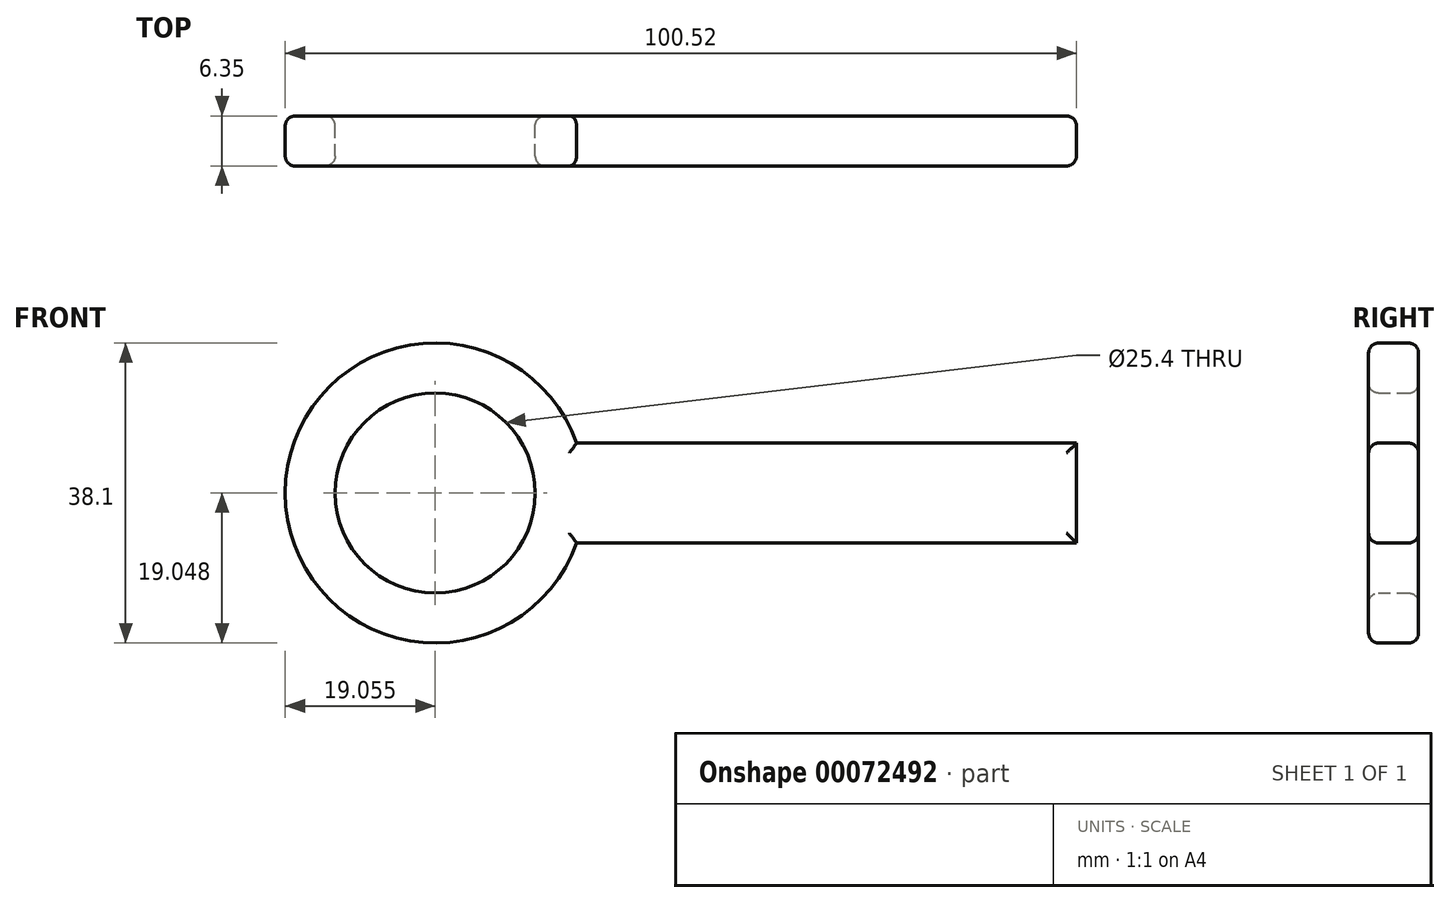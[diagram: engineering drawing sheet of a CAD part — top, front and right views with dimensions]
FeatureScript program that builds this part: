
annotation { "Feature Type Name" : "Feature", "Feature Type Description" : "" }
export const myFeature = defineFeature(function(context is Context, id is Id, definition is map)
    precondition{}
    {
        {
            var Q0;
            Q0=qCreatedBy(makeId("Front.planeOp"),FACE);
            var sketch = newSketch(context, id + "F0", { "sketchPlane" : qUnion([Q0])});
            skCircle(sketch, "E0", {"center": v(-45.07, 42.75) * mm, "radius": 19.05 * mm});
            skLineSegment(sketch, "E1", {"start": v(-27.1, 36.4) * mm, "end": v(36.4, 36.4) * mm});
            skLineSegment(sketch, "E2", {"start": v(-27.1, 49.1) * mm, "end": v(36.4, 49.1) * mm});
            skLineSegment(sketch, "E3", {"start": v(36.4, 49.1) * mm, "end": v(36.4, 36.4) * mm});
            skCircle(sketch, "E4", {"center": v(-45.07, 42.75) * mm, "radius": 12.7 * mm});
            skLineSegment(sketch, "E5.bottom", {"start": v(26.7, 36.4) * mm, "end": v(20.35, 36.4) * mm});
            skLineSegment(sketch, "E5.top", {"start": v(26.7, 17.35) * mm, "end": v(20.35, 17.35) * mm});
            skLineSegment(sketch, "E5.left", {"start": v(26.7, 36.4) * mm, "end": v(26.7, 17.35) * mm});
            skLineSegment(sketch, "E5.right", {"start": v(20.35, 36.4) * mm, "end": v(20.35, 17.35) * mm});
            skPoint(sketch, "E6.oppositeSnap0", {"position": v(4.65, 36.4) * mm});
            skLineSegment(sketch, "E6.bottom", {"start": v(11, 36.4) * mm, "end": v(4.65, 36.4) * mm});
            skLineSegment(sketch, "E6.top", {"start": v(11, 17.35) * mm, "end": v(4.65, 17.35) * mm});
            skLineSegment(sketch, "E6.left", {"start": v(11, 36.4) * mm, "end": v(11, 17.35) * mm});
            skLineSegment(sketch, "E6.right", {"start": v(4.65, 36.4) * mm, "end": v(4.65, 17.35) * mm});
            skSolve(sketch);
        }
        {
            var Q0;
            Q0=makeQuery(id+"F0.imprint","IMPRINT",FACE,{"disambiguationData":[TD([[makeQuery(id+"F0.imprint","IMPRINT",EDGE,{"derivedFrom":sQuery(id+"F0.wireOp",EDGE,"E5.bottom")}),1.0]])]});
            var Q1;
            Q1=makeQuery(id+"F0.imprint","IMPRINT",FACE,{"disambiguationData":[TD([[makeQuery(id+"F0.imprint","IMPRINT",EDGE,{"derivedFrom":sQuery(id+"F0.wireOp",EDGE,"E4")}),-1.0]])]});
            var Q2;
            {var subQ6=sQuery(id+"F0.wireOp",EDGE,"E2");Q2=makeQuery(id+"F0.imprint","IMPRINT",FACE,{"disambiguationData":[TD([[makeQuery(id+"F0.imprint","IMPRINT",EDGE,{"derivedFrom":subQ6}),-1.0]])]});}
            var Q3;
            Q3=makeQuery(id+"F0.imprint","IMPRINT",FACE,{"disambiguationData":[TD([[makeQuery(id+"F0.imprint","IMPRINT",EDGE,{"derivedFrom":sQuery(id+"F0.wireOp",EDGE,"E6.bottom")}),1.0]])]});
            extrude(context, id + "F1", {"entities" : qUnion([Q0, Q1, Q2, Q3]), "depth" : 6.35 * mm});
        }
        {
            var Q0;
            Q0=makeQuery(id+"F1.opExtrude","CAP_EDGE",EDGE,{"disambiguationData":[OSD([sQuery(id+"F0.wireOp",EDGE,"E4")])],"isStart":false});
            var Q1;
            Q1=makeQuery(id+"F1.opExtrude","CAP_EDGE",EDGE,{"disambiguationData":[OSD([sQuery(id+"F0.wireOp",EDGE,"E4")])],"isStart":true});
            fillet(context, id + "F2", {"entities" : qUnion([Q0, Q1]), "radius" : 1.27 * mm, "tangentPropagation" : true, "allowEdgeOverflow" : false});
        }
        {
            var Q0;
            Q0=makeQuery(id+"F1.opExtrude","CAP_EDGE",EDGE,{"disambiguationData":[OSD([sQuery(id+"F0.wireOp",EDGE,"E0")])],"isStart":false});
            fillet(context, id + "F3", {"entities" : qUnion([Q0]), "radius" : 1.27 * mm, "tangentPropagation" : true, "allowEdgeOverflow" : false});
        }
        {
            var Q0;
            Q0=makeQuery(id+"F1.opExtrude","CAP_EDGE",EDGE,{"disambiguationData":[OSD([sQuery(id+"F0.wireOp",EDGE,"E0")])],"isStart":true});
            fillet(context, id + "F4", {"entities" : qUnion([Q0]), "radius" : 1.27 * mm, "tangentPropagation" : true, "allowEdgeOverflow" : false});
        }
        {
            var Q0;
            Q0=makeQuery(id+"F1.opExtrude","CAP_EDGE",EDGE,{"disambiguationData":[OSD([sQuery(id+"F0.wireOp",EDGE,"E2")])],"isStart":true});
            var Q1;
            {var subQ0=sQuery(id+"F0.wireOp",EDGE,"E1");Q1=makeQuery(id+"F1.opExtrude","CAP_EDGE",EDGE,{"disambiguationData":[OSD([subQ0]),TDD([makeQuery(id+"F0.imprint","IMPRINT",EDGE,{"disambiguationData":[TD([[makeQuery(id+"F0.imprint","INTERSECT",VERTEX,{"derivedFrom":[subQ0,sQuery(id+"F0.wireOp",EDGE,"E5.bottom"),sQuery(id+"F0.wireOp",EDGE,"E5.right")]}),1.0]])],"derivedFrom":subQ0})])],"isStart":true});}
            var Q2;
            {var subQ0=sQuery(id+"F0.wireOp",EDGE,"E1");Q2=makeQuery(id+"F1.opExtrude","CAP_EDGE",EDGE,{"disambiguationData":[OSD([subQ0]),TDD([makeQuery(id+"F0.imprint","IMPRINT",EDGE,{"disambiguationData":[TD([[makeQuery(id+"F0.imprint","INTERSECT",VERTEX,{"derivedFrom":[sQuery(id+"F0.wireOp",EDGE,"E0"),subQ0]}),-1.0]])],"derivedFrom":subQ0})])],"isStart":true});}
            var Q3;
            {var subQ0=sQuery(id+"F0.wireOp",EDGE,"E1");Q3=makeQuery(id+"F1.opExtrude","CAP_EDGE",EDGE,{"disambiguationData":[OSD([subQ0]),TDD([makeQuery(id+"F0.imprint","IMPRINT",EDGE,{"disambiguationData":[TD([[makeQuery(id+"F0.imprint","INTERSECT",VERTEX,{"derivedFrom":[subQ0,sQuery(id+"F0.wireOp",EDGE,"E3")]}),1.0]])],"derivedFrom":subQ0})])],"isStart":true});}
            var Q4;
            Q4=makeQuery(id+"F1.opExtrude","CAP_EDGE",EDGE,{"disambiguationData":[OSD([sQuery(id+"F0.wireOp",EDGE,"E3")])],"isStart":true});
            var Q5;
            Q5=makeQuery(id+"F1.opExtrude","CAP_EDGE",EDGE,{"disambiguationData":[OSD([sQuery(id+"F0.wireOp",EDGE,"E5.left")])],"isStart":true});
            var Q6;
            Q6=makeQuery(id+"F1.opExtrude","CAP_EDGE",EDGE,{"disambiguationData":[OSD([sQuery(id+"F0.wireOp",EDGE,"E5.top")])],"isStart":true});
            var Q7;
            Q7=makeQuery(id+"F1.opExtrude","CAP_EDGE",EDGE,{"disambiguationData":[OSD([sQuery(id+"F0.wireOp",EDGE,"E5.right")])],"isStart":true});
            var Q8;
            Q8=makeQuery(id+"F1.opExtrude","CAP_EDGE",EDGE,{"disambiguationData":[OSD([sQuery(id+"F0.wireOp",EDGE,"E6.left")])],"isStart":true});
            var Q9;
            Q9=makeQuery(id+"F1.opExtrude","CAP_EDGE",EDGE,{"disambiguationData":[OSD([sQuery(id+"F0.wireOp",EDGE,"E6.top")])],"isStart":true});
            var Q10;
            Q10=makeQuery(id+"F1.opExtrude","CAP_EDGE",EDGE,{"disambiguationData":[OSD([sQuery(id+"F0.wireOp",EDGE,"E6.right")])],"isStart":true});
            fillet(context, id + "F5", {"entities" : qUnion([Q0, Q1, Q2, Q3, Q4, Q5, Q6, Q7, Q8, Q9, Q10]), "radius" : 1.27 * mm, "tangentPropagation" : true, "allowEdgeOverflow" : false});
        }
        {
            var Q0;
            Q0=makeQuery(id+"F1.opExtrude","CAP_EDGE",EDGE,{"disambiguationData":[OSD([sQuery(id+"F0.wireOp",EDGE,"E2")])],"isStart":false});
            var Q1;
            Q1=makeQuery(id+"F1.opExtrude","CAP_EDGE",EDGE,{"disambiguationData":[OSD([sQuery(id+"F0.wireOp",EDGE,"E6.right")])],"isStart":false});
            var Q2;
            Q2=makeQuery(id+"F1.opExtrude","CAP_EDGE",EDGE,{"disambiguationData":[OSD([sQuery(id+"F0.wireOp",EDGE,"E6.top")])],"isStart":false});
            var Q3;
            Q3=makeQuery(id+"F1.opExtrude","CAP_EDGE",EDGE,{"disambiguationData":[OSD([sQuery(id+"F0.wireOp",EDGE,"E6.left")])],"isStart":false});
            var Q4;
            {var subQ0=sQuery(id+"F0.wireOp",EDGE,"E1");Q4=makeQuery(id+"F1.opExtrude","CAP_EDGE",EDGE,{"disambiguationData":[OSD([subQ0]),TDD([makeQuery(id+"F0.imprint","IMPRINT",EDGE,{"disambiguationData":[TD([[makeQuery(id+"F0.imprint","INTERSECT",VERTEX,{"derivedFrom":[sQuery(id+"F0.wireOp",EDGE,"E0"),subQ0]}),-1.0]])],"derivedFrom":subQ0})])],"isStart":false});}
            var Q5;
            {var subQ0=sQuery(id+"F0.wireOp",EDGE,"E1");Q5=makeQuery(id+"F1.opExtrude","CAP_EDGE",EDGE,{"disambiguationData":[OSD([subQ0]),TDD([makeQuery(id+"F0.imprint","IMPRINT",EDGE,{"disambiguationData":[TD([[makeQuery(id+"F0.imprint","INTERSECT",VERTEX,{"derivedFrom":[subQ0,sQuery(id+"F0.wireOp",EDGE,"E5.bottom"),sQuery(id+"F0.wireOp",EDGE,"E5.right")]}),1.0]])],"derivedFrom":subQ0})])],"isStart":false});}
            var Q6;
            Q6=makeQuery(id+"F1.opExtrude","CAP_EDGE",EDGE,{"disambiguationData":[OSD([sQuery(id+"F0.wireOp",EDGE,"E5.right")])],"isStart":false});
            var Q7;
            Q7=makeQuery(id+"F1.opExtrude","CAP_EDGE",EDGE,{"disambiguationData":[OSD([sQuery(id+"F0.wireOp",EDGE,"E5.top")])],"isStart":false});
            var Q8;
            Q8=makeQuery(id+"F1.opExtrude","CAP_EDGE",EDGE,{"disambiguationData":[OSD([sQuery(id+"F0.wireOp",EDGE,"E5.left")])],"isStart":false});
            var Q9;
            {var subQ0=sQuery(id+"F0.wireOp",EDGE,"E1");Q9=makeQuery(id+"F1.opExtrude","CAP_EDGE",EDGE,{"disambiguationData":[OSD([subQ0]),TDD([makeQuery(id+"F0.imprint","IMPRINT",EDGE,{"disambiguationData":[TD([[makeQuery(id+"F0.imprint","INTERSECT",VERTEX,{"derivedFrom":[subQ0,sQuery(id+"F0.wireOp",EDGE,"E3")]}),1.0]])],"derivedFrom":subQ0})])],"isStart":false});}
            var Q10;
            Q10=makeQuery(id+"F1.opExtrude","CAP_EDGE",EDGE,{"disambiguationData":[OSD([sQuery(id+"F0.wireOp",EDGE,"E3")])],"isStart":false});
            fillet(context, id + "F6", {"entities" : qUnion([Q0, Q1, Q2, Q3, Q4, Q5, Q6, Q7, Q8, Q9, Q10]), "radius" : 1.27 * mm, "tangentPropagation" : true, "allowEdgeOverflow" : false});
        }
    });
